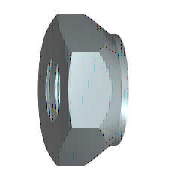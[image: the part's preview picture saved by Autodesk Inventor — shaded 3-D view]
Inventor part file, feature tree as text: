
AUTODESK INVENTOR PART (.ipt)
format: ipt  version: 2018 (Build 220112000, 112)  size: 184,320 bytes
history: native  units: mm (DEFAULTED — no unit token found)
features: sketch x3, hole x1, chamfer x1, other x1, plane x1
ambient origin geometry x7: Origin, YZ Plane, XZ Plane, X Axis, Y Axis, Z Axis, Center Point
bodies: Solid1 (feature_tree), Body (feature_tree)
feature tree (7):
  hole  "Thread"  [1 undecoded]
  chamfer  "Chamfer3"  Distance=7.0mm
  other  "Work Axis1"
  plane  "Work Plane1"
  sketch  "Sketch1"  dims[d0=8.082904mm d1=4.0mm]
  sketch  "Sketch3"  dims[d3=30.0deg d5=7.0mm d6=5.95mm d7=90.0deg d8=8.726646mm d9=1.9mm d24=3.242mm d25=6.0mm d26=4.0mm d27=2.0mm d28=14.3117mm d29=8.0mm d30=20.594885mm d10=0.378886mm d11=30.0deg d12=0.378886mm d13=30.0deg d14=0.0mm d38=0.0mm d39=0.378886mm d40=0.378886mm d41=0.0mm d42=0.0mm]
  sketch  "Sketch2"  dims[d2=0.0mm]
note: 1 required parameter value undecoded (feature->parameter linkage not recoverable at this tier; creation-order binding heuristic only, values carry confidence <= 0.55)
